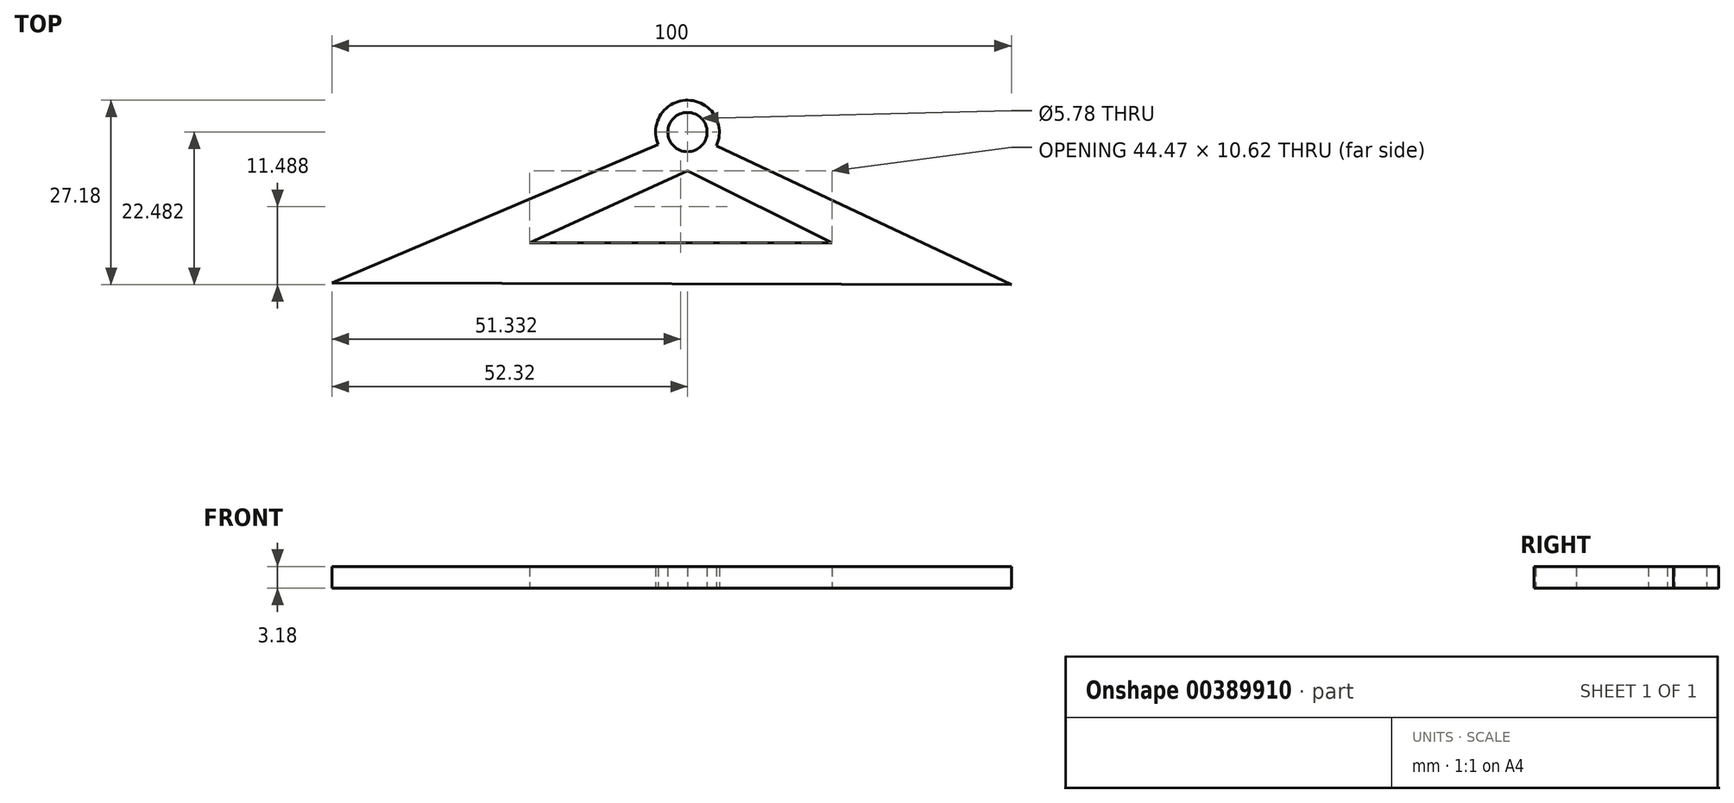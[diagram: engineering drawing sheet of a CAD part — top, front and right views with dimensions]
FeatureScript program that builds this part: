
annotation { "Feature Type Name" : "Feature", "Feature Type Description" : "" }
export const myFeature = defineFeature(function(context is Context, id is Id, definition is map)
    precondition{}
    {
        {
            var Q0;
            Q0=qCreatedBy(makeId("Top.planeOp"),FACE);
            var sketch = newSketch(context, id + "F0", { "sketchPlane" : qUnion([Q0])});
            skLineSegment(sketch, "E0", {"start": v(-52.32, 12.48) * mm, "end": v(0, 34.71) * mm});
            skLineSegment(sketch, "E1", {"start": v(0, 34.71) * mm, "end": v(47.68, 12.23) * mm});
            skLineSegment(sketch, "E2", {"start": v(47.68, 12.23) * mm, "end": v(-52.32, 12.48) * mm});
            skLineSegment(sketch, "E3", {"start": v(-23.22, 18.4) * mm, "end": v(0, 29.03) * mm});
            skLineSegment(sketch, "E4", {"start": v(0, 29.03) * mm, "end": v(21.25, 18.4) * mm});
            skLineSegment(sketch, "E5", {"start": v(21.25, 18.4) * mm, "end": v(-23.22, 18.4) * mm});
            skCircle(sketch, "E6", {"center": v(0, 34.71) * mm, "radius": 4.7 * mm});
            skCircle(sketch, "E7", {"center": v(0, 34.71) * mm, "radius": 2.9 * mm});
            skSolve(sketch);
        }
        {
            var Q0;
            Q0 = qSketchRegion(id + "F0", true);
            extrude(context, id + "F1", {"entities" : qUnion([Q0]), "depth" : 3.17 * mm});
        }
    });
